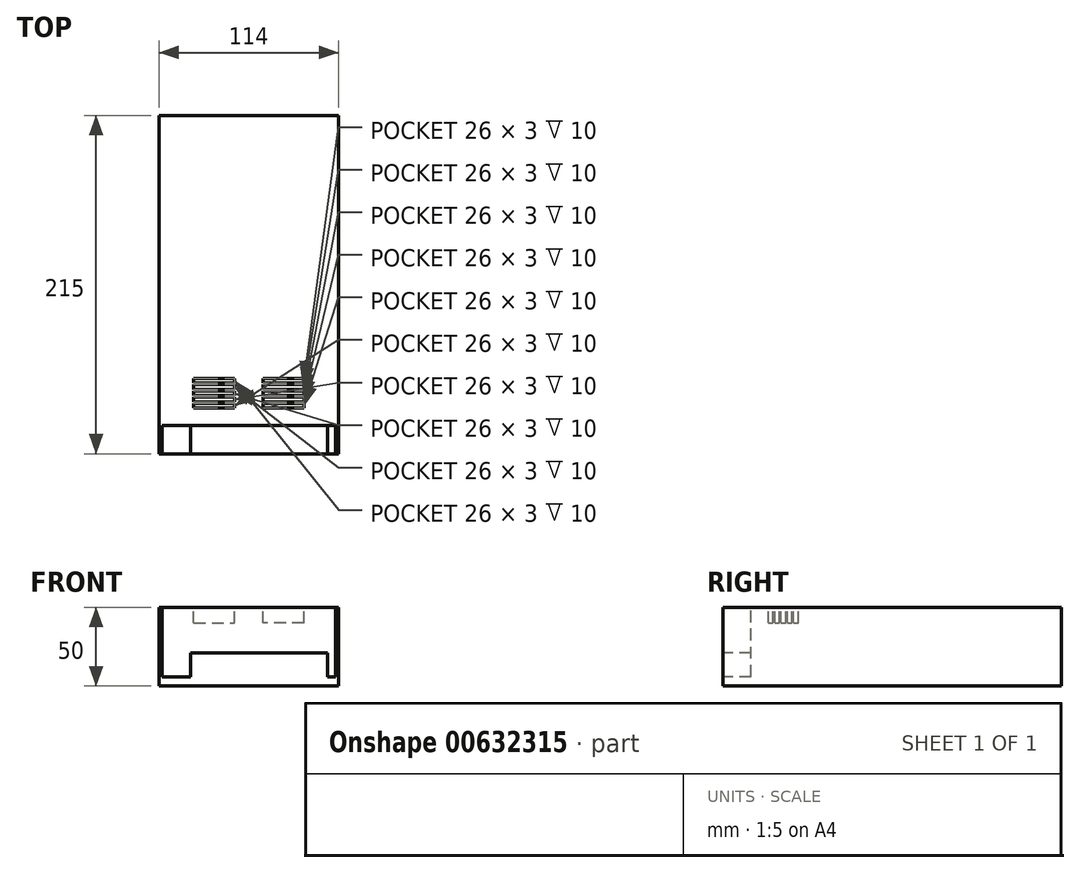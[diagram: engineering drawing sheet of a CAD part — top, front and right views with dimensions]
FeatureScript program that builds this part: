
annotation { "Feature Type Name" : "Feature", "Feature Type Description" : "" }
export const myFeature = defineFeature(function(context is Context, id is Id, definition is map)
    precondition{}
    {
        {
            var Q0;
            Q0=qCreatedBy(makeId("Right.planeOp"),FACE);
            var sketch = newSketch(context, id + "F0", { "sketchPlane" : qUnion([Q0])});
            skLineSegment(sketch, "E0", {"start": v(0, 0) * mm, "end": v(-215, 0) * mm});
            skLineSegment(sketch, "E1", {"start": v(-215, 0) * mm, "end": v(-215, 50) * mm});
            skLineSegment(sketch, "E2", {"start": v(-215, 50) * mm, "end": v(0, 50) * mm});
            skLineSegment(sketch, "E3", {"start": v(0, 50) * mm, "end": v(0, 0) * mm});
            skSolve(sketch);
        }
        {
            var Q0;
            Q0=makeQuery(id+"F0.imprint","IMPRINT",FACE,{"disambiguationData":[TD([[makeQuery(id+"F0.imprint","IMPRINT",EDGE,{"derivedFrom":sQuery(id+"F0.wireOp",EDGE,"E0")}),-1.0]])]});
            extrude(context, id + "F1", {"entities" : qUnion([Q0]), "endBound" : BoundingType.SYMMETRIC, "depth" : 114 * mm, "offsetDistance" : 25 * mm});
        }
        {
            var Q0;
            Q0=makeQuery(id+"F1.opExtrude","SWEPT_FACE",FACE,{"disambiguationData":[OSD([sQuery(id+"F0.wireOp",EDGE,"E1")])]});
            var sketch = newSketch(context, id + "F2", { "sketchPlane" : qUnion([Q0])});
            skLineSegment(sketch, "E4.bottom", {"start": v(-57, 0) * mm, "end": v(57, 0) * mm});
            skLineSegment(sketch, "E4.top", {"start": v(-57, 0) * mm, "end": v(57, 0) * mm});
            skLineSegment(sketch, "E4.left", {"start": v(-57, 0) * mm, "end": v(-57, 0) * mm});
            skLineSegment(sketch, "E4.right", {"start": v(57, 0) * mm, "end": v(57, 0) * mm});
            skLineSegment(sketch, "E5.top", {"start": v(-57, 6) * mm, "end": v(57, 6) * mm});
            skLineSegment(sketch, "E5.left", {"start": v(-57, 0) * mm, "end": v(-57, 6) * mm});
            skLineSegment(sketch, "E5.right", {"start": v(57, 0) * mm, "end": v(57, 6) * mm});
            skLineSegment(sketch, "E6.bottom", {"start": v(-57, 6) * mm, "end": v(-55, 6) * mm});
            skLineSegment(sketch, "E6.top", {"start": v(-57, 50) * mm, "end": v(-55, 50) * mm});
            skLineSegment(sketch, "E6.left", {"start": v(-57, 6) * mm, "end": v(-57, 50) * mm});
            skLineSegment(sketch, "E6.right", {"start": v(-55, 6) * mm, "end": v(-55, 50) * mm});
            skLineSegment(sketch, "E7.bottom", {"start": v(57, 6) * mm, "end": v(55, 6) * mm});
            skLineSegment(sketch, "E7.top", {"start": v(57, 50) * mm, "end": v(55, 50) * mm});
            skLineSegment(sketch, "E7.left", {"start": v(57, 6) * mm, "end": v(57, 50) * mm});
            skLineSegment(sketch, "E7.right", {"start": v(55, 6) * mm, "end": v(55, 50) * mm});
            skLineSegment(sketch, "E8", {"start": v(50, 6) * mm, "end": v(50, 50) * mm, "construction": true});
            skLineSegment(sketch, "E9.bottom", {"start": v(50, 6) * mm, "end": v(-37, 6) * mm});
            skLineSegment(sketch, "E9.top", {"start": v(50, 21) * mm, "end": v(-37, 21) * mm});
            skLineSegment(sketch, "E9.left", {"start": v(50, 6) * mm, "end": v(50, 21) * mm});
            skLineSegment(sketch, "E9.right", {"start": v(-37, 6) * mm, "end": v(-37, 21) * mm});
            skSolve(sketch);
        }
        {
            var Q0;
            {var subQ0=sQuery(id+"F2.wireOp",EDGE,"E6.right");Q0=makeQuery(id+"F2.imprint","IMPRINT",FACE,{"disambiguationData":[TD([[makeQuery(id+"F2.imprint","IMPRINT",EDGE,{"derivedFrom":subQ0}),-1.0]])]});}
            extrude(context, id + "F3", {"entities" : qUnion([Q0]), "operationType" : NewBodyOperationType.REMOVE, "oppositeDirection" : true, "depth" : 18 * mm, "offsetDistance" : 25 * mm});
        }
        {
            var Q0;
            Q0=makeQuery(id+"F1.opExtrude","SWEPT_FACE",FACE,{"disambiguationData":[OSD([sQuery(id+"F0.wireOp",EDGE,"E2")])]});
            var sketch = newSketch(context, id + "F4", { "sketchPlane" : qUnion([Q0])});
            skLineSegment(sketch, "E10.bottom", {"start": v(35, -186) * mm, "end": v(9, -186) * mm});
            skLineSegment(sketch, "E10.top", {"start": v(35, -183) * mm, "end": v(9, -183) * mm});
            skLineSegment(sketch, "E10.left", {"start": v(35, -186) * mm, "end": v(35, -183) * mm});
            skLineSegment(sketch, "E10.right", {"start": v(9, -186) * mm, "end": v(9, -183) * mm});
            skLineSegment(sketch, "E11.0.1.0", {"start": v(9, -182) * mm, "end": v(9, -179) * mm});
            skLineSegment(sketch, "E11.0.1.1", {"start": v(35, -182) * mm, "end": v(9, -182) * mm});
            skLineSegment(sketch, "E11.0.1.2", {"start": v(35, -179) * mm, "end": v(9, -179) * mm});
            skLineSegment(sketch, "E11.0.1.3", {"start": v(35, -182) * mm, "end": v(35, -179) * mm});
            skLineSegment(sketch, "E11.0.2.0", {"start": v(9, -178) * mm, "end": v(9, -175) * mm});
            skLineSegment(sketch, "E11.0.2.1", {"start": v(35, -178) * mm, "end": v(9, -178) * mm});
            skLineSegment(sketch, "E11.0.2.2", {"start": v(35, -175) * mm, "end": v(9, -175) * mm});
            skLineSegment(sketch, "E11.0.2.3", {"start": v(35, -178) * mm, "end": v(35, -175) * mm});
            skLineSegment(sketch, "E11.0.3.0", {"start": v(9, -174) * mm, "end": v(9, -171) * mm});
            skLineSegment(sketch, "E11.0.3.1", {"start": v(35, -174) * mm, "end": v(9, -174) * mm});
            skLineSegment(sketch, "E11.0.3.2", {"start": v(35, -171) * mm, "end": v(9, -171) * mm});
            skLineSegment(sketch, "E11.0.3.3", {"start": v(35, -174) * mm, "end": v(35, -171) * mm});
            skLineSegment(sketch, "E11.0.4.0", {"start": v(9, -170) * mm, "end": v(9, -167) * mm});
            skLineSegment(sketch, "E11.0.4.1", {"start": v(35, -170) * mm, "end": v(9, -170) * mm});
            skLineSegment(sketch, "E11.0.4.2", {"start": v(35, -167) * mm, "end": v(9, -167) * mm});
            skLineSegment(sketch, "E11.0.4.3", {"start": v(35, -170) * mm, "end": v(35, -167) * mm});
            skLineSegment(sketch, "E11.direction1", {"start": v(9, -186) * mm, "end": v(34, -186) * mm, "construction": true});
            skLineSegment(sketch, "E11.direction2", {"start": v(9, -186) * mm, "end": v(9, -182) * mm, "construction": true});
            skLineSegment(sketch, "E12.MirrorCS", {"start": v(-9, -186) * mm, "end": v(-34, -186) * mm, "construction": true});
            skLineSegment(sketch, "E13.MirrorCS", {"start": v(-9, -186) * mm, "end": v(-9, -182) * mm, "construction": true});
            skLineSegment(sketch, "E14.MirrorCS", {"start": v(-9, -182) * mm, "end": v(-9, -179) * mm});
            skLineSegment(sketch, "E15.MirrorCS", {"start": v(-9, -186) * mm, "end": v(-9, -183) * mm});
            skLineSegment(sketch, "E16.MirrorCS", {"start": v(-9, -174) * mm, "end": v(-9, -171) * mm});
            skLineSegment(sketch, "E17.MirrorCS", {"start": v(-35, -178) * mm, "end": v(-35, -175) * mm});
            skLineSegment(sketch, "E18.MirrorCS", {"start": v(-9, -178) * mm, "end": v(-9, -175) * mm});
            skLineSegment(sketch, "E19.MirrorCS", {"start": v(-35, -182) * mm, "end": v(-35, -179) * mm});
            skLineSegment(sketch, "E20.MirrorCS", {"start": v(-35, -186) * mm, "end": v(-35, -183) * mm});
            skLineSegment(sketch, "E21.MirrorCS", {"start": v(-35, -174) * mm, "end": v(-35, -171) * mm});
            skLineSegment(sketch, "E22.MirrorCS", {"start": v(-9, -170) * mm, "end": v(-9, -167) * mm});
            skLineSegment(sketch, "E23.MirrorCS", {"start": v(-35, -170) * mm, "end": v(-35, -167) * mm});
            skLineSegment(sketch, "E24.MirrorCS", {"start": v(-35, -186) * mm, "end": v(-9, -186) * mm});
            skLineSegment(sketch, "E25.MirrorCS", {"start": v(-35, -170) * mm, "end": v(-9, -170) * mm});
            skLineSegment(sketch, "E26.MirrorCS", {"start": v(-35, -175) * mm, "end": v(-9, -175) * mm});
            skLineSegment(sketch, "E27.MirrorCS", {"start": v(-35, -178) * mm, "end": v(-9, -178) * mm});
            skLineSegment(sketch, "E28.MirrorCS", {"start": v(-35, -179) * mm, "end": v(-9, -179) * mm});
            skLineSegment(sketch, "E29.MirrorCS", {"start": v(-35, -182) * mm, "end": v(-9, -182) * mm});
            skLineSegment(sketch, "E30.MirrorCS", {"start": v(-35, -183) * mm, "end": v(-9, -183) * mm});
            skLineSegment(sketch, "E31.MirrorCS", {"start": v(-35, -171) * mm, "end": v(-9, -171) * mm});
            skLineSegment(sketch, "E32.MirrorCS", {"start": v(-35, -174) * mm, "end": v(-9, -174) * mm});
            skLineSegment(sketch, "E33.MirrorCS", {"start": v(-35, -167) * mm, "end": v(-9, -167) * mm});
            skSolve(sketch);
        }
        {
            var Q0;
            Q0=makeQuery(id+"F4.imprint","IMPRINT",FACE,{"disambiguationData":[TD([[makeQuery(id+"F4.imprint","IMPRINT",EDGE,{"derivedFrom":sQuery(id+"F4.wireOp",EDGE,"E11.0.4.0")}),-1.0]])]});
            var Q1;
            Q1=makeQuery(id+"F4.imprint","IMPRINT",FACE,{"disambiguationData":[TD([[makeQuery(id+"F4.imprint","IMPRINT",EDGE,{"derivedFrom":sQuery(id+"F4.wireOp",EDGE,"E11.0.3.0")}),-1.0]])]});
            var Q2;
            Q2=makeQuery(id+"F4.imprint","IMPRINT",FACE,{"disambiguationData":[TD([[makeQuery(id+"F4.imprint","IMPRINT",EDGE,{"derivedFrom":sQuery(id+"F4.wireOp",EDGE,"E11.0.2.0")}),-1.0]])]});
            var Q3;
            Q3=makeQuery(id+"F4.imprint","IMPRINT",FACE,{"disambiguationData":[TD([[makeQuery(id+"F4.imprint","IMPRINT",EDGE,{"derivedFrom":sQuery(id+"F4.wireOp",EDGE,"E11.0.1.0")}),-1.0]])]});
            var Q4;
            Q4=makeQuery(id+"F4.imprint","IMPRINT",FACE,{"disambiguationData":[TD([[makeQuery(id+"F4.imprint","IMPRINT",EDGE,{"derivedFrom":sQuery(id+"F4.wireOp",EDGE,"E10.bottom")}),-1.0]])]});
            var Q5;
            Q5=makeQuery(id+"F4.imprint","IMPRINT",FACE,{"disambiguationData":[TD([[makeQuery(id+"F4.imprint","IMPRINT",EDGE,{"derivedFrom":sQuery(id+"F4.wireOp",EDGE,"E15.MirrorCS")}),1.0]])]});
            var Q6;
            Q6=makeQuery(id+"F4.imprint","IMPRINT",FACE,{"disambiguationData":[TD([[makeQuery(id+"F4.imprint","IMPRINT",EDGE,{"derivedFrom":sQuery(id+"F4.wireOp",EDGE,"E14.MirrorCS")}),1.0]])]});
            var Q7;
            Q7=makeQuery(id+"F4.imprint","IMPRINT",FACE,{"disambiguationData":[TD([[makeQuery(id+"F4.imprint","IMPRINT",EDGE,{"derivedFrom":sQuery(id+"F4.wireOp",EDGE,"E17.MirrorCS")}),-1.0]])]});
            var Q8;
            Q8=makeQuery(id+"F4.imprint","IMPRINT",FACE,{"disambiguationData":[TD([[makeQuery(id+"F4.imprint","IMPRINT",EDGE,{"derivedFrom":sQuery(id+"F4.wireOp",EDGE,"E16.MirrorCS")}),1.0]])]});
            var Q9;
            Q9=makeQuery(id+"F4.imprint","IMPRINT",FACE,{"disambiguationData":[TD([[makeQuery(id+"F4.imprint","IMPRINT",EDGE,{"derivedFrom":sQuery(id+"F4.wireOp",EDGE,"E22.MirrorCS")}),1.0]])]});
            extrude(context, id + "F5", {"entities" : qUnion([Q0, Q1, Q2, Q3, Q4, Q5, Q6, Q7, Q8, Q9]), "operationType" : NewBodyOperationType.REMOVE, "oppositeDirection" : true, "depth" : 10 * mm, "offsetDistance" : 25 * mm});
        }
    });
